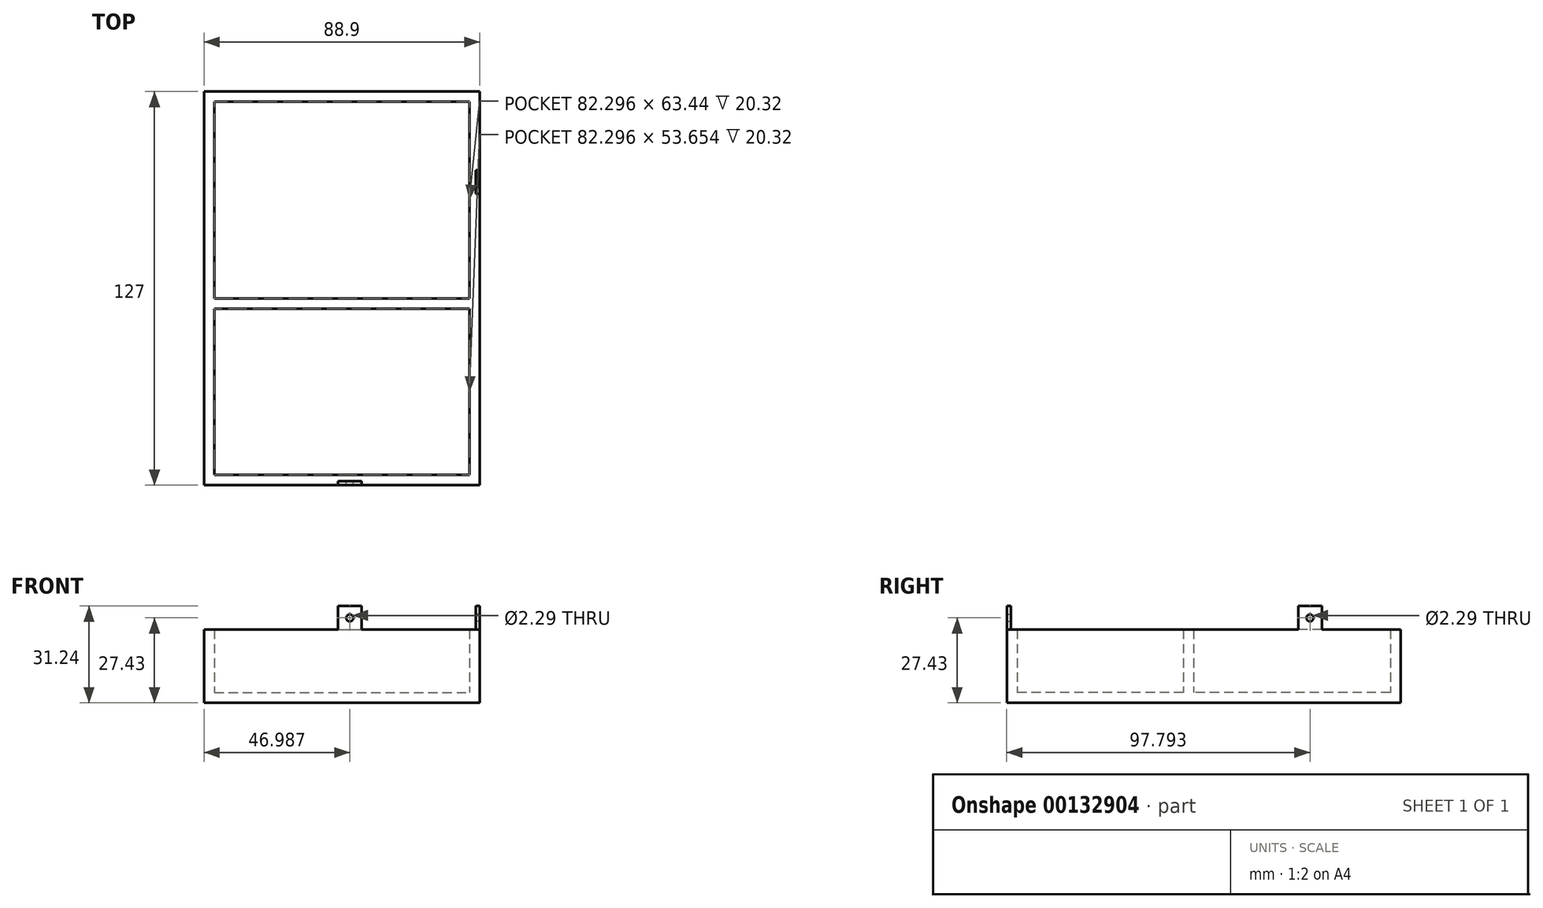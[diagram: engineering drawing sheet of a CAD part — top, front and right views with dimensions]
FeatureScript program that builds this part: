
annotation { "Feature Type Name" : "Feature", "Feature Type Description" : "" }
export const myFeature = defineFeature(function(context is Context, id is Id, definition is map)
    precondition{}
    {
        {
            var Q0;
            Q0=qCreatedBy(makeId("Top.planeOp"),FACE);
            var sketch = newSketch(context, id + "F0", { "sketchPlane" : qUnion([Q0])});
            skLineSegment(sketch, "E0.bottom", {"start": v(-62.17, 63.1) * mm, "end": v(26.73, 63.1) * mm});
            skLineSegment(sketch, "E0.top", {"start": v(-62.17, -63.9) * mm, "end": v(26.73, -63.9) * mm});
            skLineSegment(sketch, "E0.left", {"start": v(-62.17, 63.1) * mm, "end": v(-62.17, -63.9) * mm});
            skLineSegment(sketch, "E0.right", {"start": v(26.73, 63.1) * mm, "end": v(26.73, -63.9) * mm});
            skLineSegment(sketch, "E1.bottom", {"start": v(-58.87, 59.8) * mm, "end": v(23.43, 59.8) * mm});
            skLineSegment(sketch, "E1.top", {"start": v(-58.87, -3.64) * mm, "end": v(23.43, -3.64) * mm});
            skLineSegment(sketch, "E1.left", {"start": v(-58.87, 59.8) * mm, "end": v(-58.87, -3.64) * mm});
            skLineSegment(sketch, "E1.right", {"start": v(23.43, 59.8) * mm, "end": v(23.43, -3.64) * mm});
            skLineSegment(sketch, "E2.bottom", {"start": v(-58.87, -6.94) * mm, "end": v(23.43, -6.94) * mm});
            skLineSegment(sketch, "E2.top", {"start": v(-58.87, -60.6) * mm, "end": v(23.43, -60.6) * mm});
            skLineSegment(sketch, "E2.left", {"start": v(-58.87, -6.94) * mm, "end": v(-58.87, -60.6) * mm});
            skLineSegment(sketch, "E2.right", {"start": v(23.43, -6.94) * mm, "end": v(23.43, -60.6) * mm});
            skSolve(sketch);
        }
        {
            var Q0;
            Q0 = qSketchRegion(id + "F0", true);
            extrude(context, id + "F1", {"entities" : qUnion([Q0]), "depth" : 20.32 * mm});
        }
        {
            var Q0;
            Q0=makeQuery(id+"F0.imprint","IMPRINT",FACE,{"disambiguationData":[TD([[makeQuery(id+"F0.imprint","IMPRINT",EDGE,{"derivedFrom":sQuery(id+"F0.wireOp",EDGE,"E0.bottom")}),-1.0]])]});
            var Q1;
            Q1=makeQuery(id+"F0.imprint","IMPRINT",FACE,{"disambiguationData":[TD([[makeQuery(id+"F0.imprint","IMPRINT",EDGE,{"derivedFrom":sQuery(id+"F0.wireOp",EDGE,"E1.bottom")}),-1.0]])]});
            var Q2;
            Q2=makeQuery(id+"F0.imprint","IMPRINT",FACE,{"disambiguationData":[TD([[makeQuery(id+"F0.imprint","IMPRINT",EDGE,{"derivedFrom":sQuery(id+"F0.wireOp",EDGE,"E2.bottom")}),-1.0]])]});
            extrude(context, id + "F2", {"entities" : qUnion([Q0, Q1, Q2]), "operationType" : NewBodyOperationType.ADD, "oppositeDirection" : true, "depth" : 3.3 * mm});
        }
        {
            var Q0;
            Q0=makeQuery(id+"F1.opExtrude","CAP_FACE",FACE,{"disambiguationData":[OSD([sQuery(id+"F0.wireOp",EDGE,"E0.bottom"),sQuery(id+"F0.wireOp",EDGE,"E0.top"),sQuery(id+"F0.wireOp",EDGE,"E0.left"),sQuery(id+"F0.wireOp",EDGE,"E0.right"),sQuery(id+"F0.wireOp",EDGE,"E1.bottom"),sQuery(id+"F0.wireOp",EDGE,"E1.top"),sQuery(id+"F0.wireOp",EDGE,"E1.left"),sQuery(id+"F0.wireOp",EDGE,"E1.right"),sQuery(id+"F0.wireOp",EDGE,"E2.bottom"),sQuery(id+"F0.wireOp",EDGE,"E2.top"),sQuery(id+"F0.wireOp",EDGE,"E2.left"),sQuery(id+"F0.wireOp",EDGE,"E2.right")])],"isStart":false});
            var sketch = newSketch(context, id + "F3", { "sketchPlane" : qUnion([Q0])});
            skLineSegment(sketch, "E3.bottom", {"start": v(26.73, 37.7) * mm, "end": v(25.46, 37.7) * mm});
            skLineSegment(sketch, "E3.top", {"start": v(26.73, 30.08) * mm, "end": v(25.46, 30.08) * mm});
            skLineSegment(sketch, "E3.left", {"start": v(26.73, 37.7) * mm, "end": v(26.73, 30.08) * mm});
            skLineSegment(sketch, "E3.right", {"start": v(25.46, 37.7) * mm, "end": v(25.46, 30.08) * mm});
            skLineSegment(sketch, "E4.bottom", {"start": v(-11.37, -63.9) * mm, "end": v(-19, -63.9) * mm});
            skLineSegment(sketch, "E4.top", {"start": v(-11.37, -62.63) * mm, "end": v(-19, -62.63) * mm});
            skLineSegment(sketch, "E4.left", {"start": v(-11.37, -63.9) * mm, "end": v(-11.37, -62.63) * mm});
            skLineSegment(sketch, "E4.right", {"start": v(-19, -63.9) * mm, "end": v(-19, -62.63) * mm});
            skSolve(sketch);
        }
        {
            var Q0;
            Q0 = qSketchRegion(id + "F3", true);
            extrude(context, id + "F4", {"entities" : qUnion([Q0]), "operationType" : NewBodyOperationType.ADD, "depth" : 7.62 * mm});
        }
        {
            var Q0;
            Q0=makeQuery(id+"F4.opExtrude","SWEPT_FACE",FACE,{"disambiguationData":[OSD([sQuery(id+"F3.wireOp",EDGE,"E4.top")])]});
            var sketch = newSketch(context, id + "F5", { "sketchPlane" : qUnion([Q0])});
            skCircle(sketch, "E5", {"center": v(15.18, 24.13) * mm, "radius": 1.14 * mm});
            skSolve(sketch);
        }
        {
            var Q0;
            Q0 = qSketchRegion(id + "F5", true);
            extrude(context, id + "F6", {"entities" : qUnion([Q0]), "operationType" : NewBodyOperationType.REMOVE, "endBound" : BoundingType.THROUGH_ALL, "oppositeDirection" : true, "depth" : 25.4 * mm});
        }
        {
            var Q0;
            Q0=makeQuery(id+"F4.opExtrude","SWEPT_FACE",FACE,{"disambiguationData":[OSD([sQuery(id+"F3.wireOp",EDGE,"E3.right")])]});
            var sketch = newSketch(context, id + "F7", { "sketchPlane" : qUnion([Q0])});
            skCircle(sketch, "E6", {"center": v(-33.9, 24.13) * mm, "radius": 1.14 * mm});
            skSolve(sketch);
        }
        {
            var Q0;
            Q0 = qSketchRegion(id + "F7", true);
            extrude(context, id + "F8", {"entities" : qUnion([Q0]), "operationType" : NewBodyOperationType.REMOVE, "endBound" : BoundingType.THROUGH_ALL, "oppositeDirection" : true, "depth" : 25.4 * mm});
        }
    });
